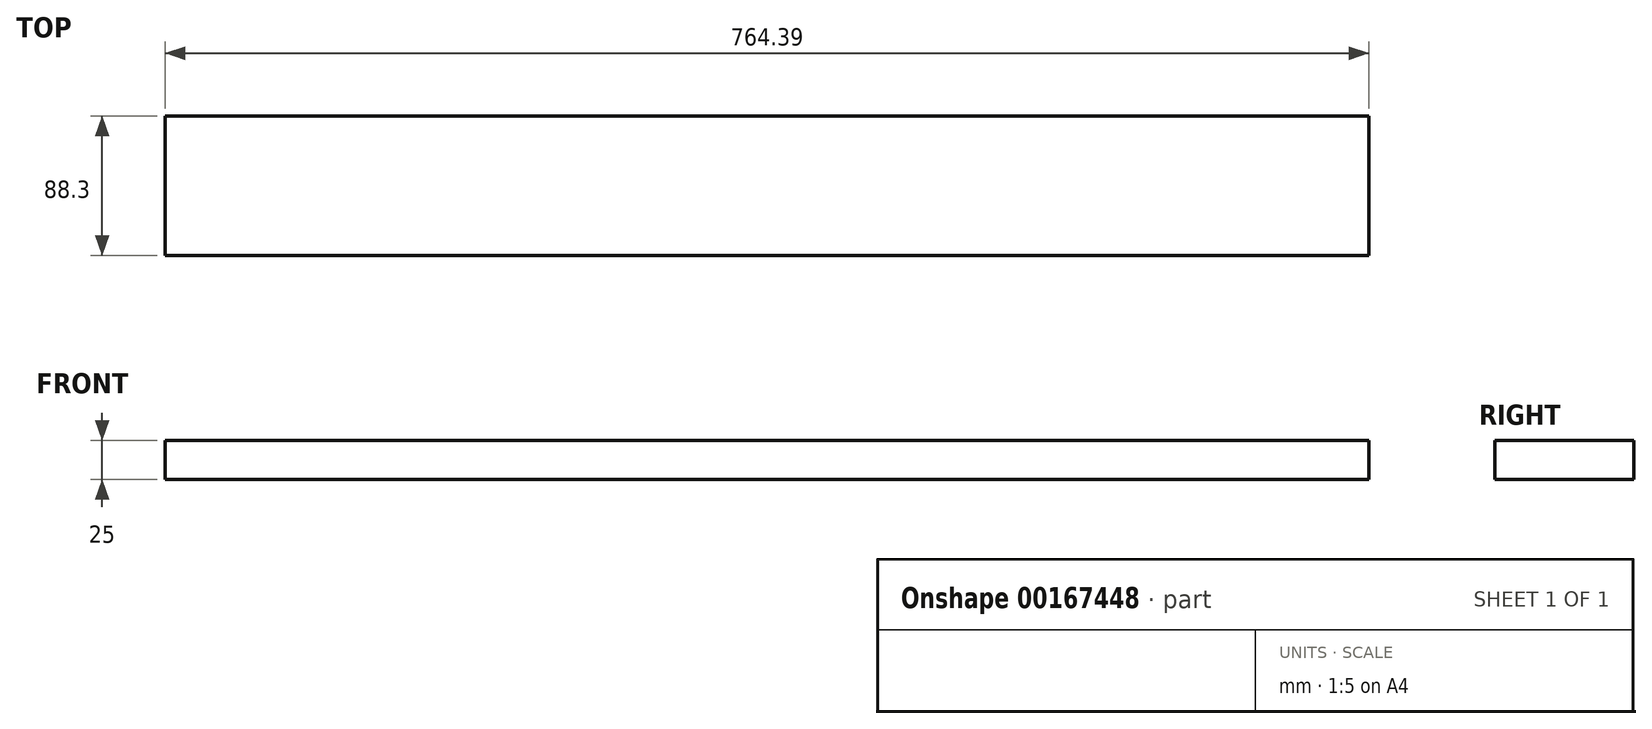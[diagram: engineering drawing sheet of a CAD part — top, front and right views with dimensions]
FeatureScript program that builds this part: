
annotation { "Feature Type Name" : "Feature", "Feature Type Description" : "" }
export const myFeature = defineFeature(function(context is Context, id is Id, definition is map)
    precondition{}
    {
        {
            var Q0;
            Q0=qCreatedBy(makeId("Top.planeOp"),FACE);
            var sketch = newSketch(context, id + "F0", { "sketchPlane" : qUnion([Q0])});
            skLineSegment(sketch, "E0.bottom", {"start": v(-411.67, 121.32) * mm, "end": v(352.72, 121.32) * mm});
            skLineSegment(sketch, "E0.top", {"start": v(-411.67, 209.62) * mm, "end": v(352.72, 209.62) * mm});
            skLineSegment(sketch, "E0.left", {"start": v(-411.67, 121.32) * mm, "end": v(-411.67, 209.62) * mm});
            skLineSegment(sketch, "E0.right", {"start": v(352.72, 121.32) * mm, "end": v(352.72, 209.62) * mm});
            skSolve(sketch);
        }
        {
            var Q0;
            Q0 = qSketchRegion(id + "F0", true);
            extrude(context, id + "F1", {"entities" : qUnion([Q0]), "depth" : 25 * mm});
        }
    });
